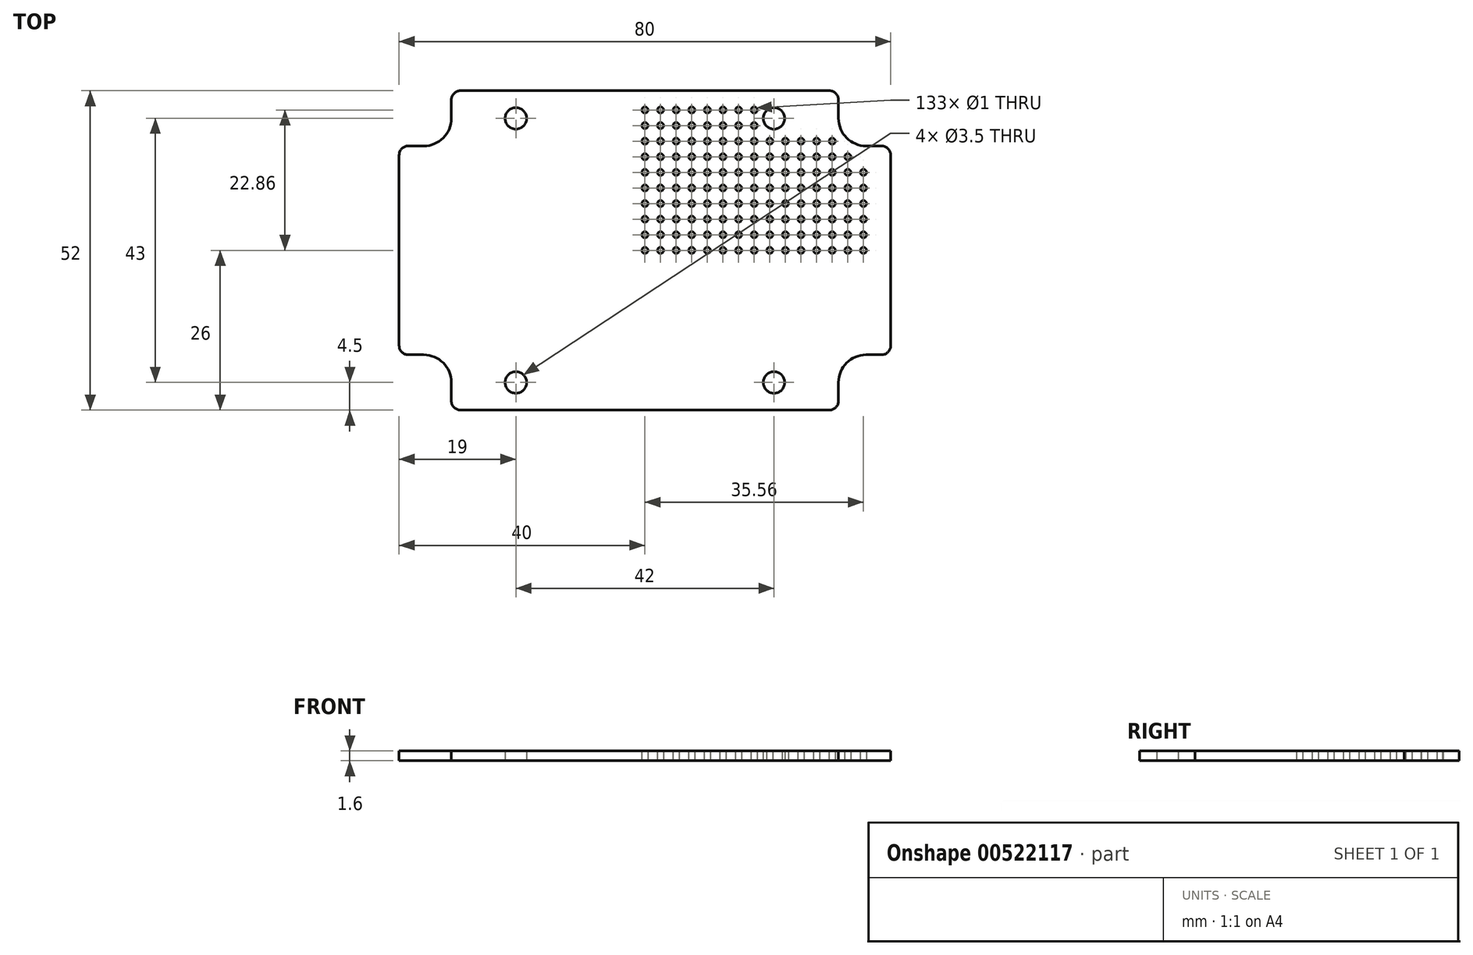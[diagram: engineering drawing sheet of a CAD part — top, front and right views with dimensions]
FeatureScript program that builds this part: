
annotation { "Feature Type Name" : "Feature", "Feature Type Description" : "" }
export const myFeature = defineFeature(function(context is Context, id is Id, definition is map)
    precondition{}
    {
        {
            var Q0;
            Q0=qCreatedBy(makeId("Top.planeOp"),FACE);
            var sketch = newSketch(context, id + "F0", { "sketchPlane" : qUnion([Q0])});
            skLineSegment(sketch, "E0.bottom", {"start": v(-31.5, 26) * mm, "end": v(31.5, 26) * mm});
            skLineSegment(sketch, "E0.top", {"start": v(-31.5, -26) * mm, "end": v(31.5, -26) * mm});
            skLineSegment(sketch, "E0.right", {"start": v(40, 17) * mm, "end": v(40, -17) * mm});
            skPoint(sketch, "E0.middle", {"position": v(0, 0) * mm});
            skLineSegment(sketch, "E1.bottom", {"start": v(-36, 21.5) * mm, "end": v(36, 21.5) * mm, "construction": true});
            skLineSegment(sketch, "E1.top", {"start": v(-36, -21.5) * mm, "end": v(36, -21.5) * mm, "construction": true});
            skLineSegment(sketch, "E1.left", {"start": v(-36, 21.5) * mm, "end": v(-36, -21.5) * mm, "construction": true});
            skLineSegment(sketch, "E1.right", {"start": v(36, 21.5) * mm, "end": v(36, -21.5) * mm, "construction": true});
            skArc(sketch, "E2", {"start": v(31.5, 21.5) * mm, "mid": v(32.82, 18.32) * mm, "end": v(36, 17) * mm});
            skArc(sketch, "E3", {"start": v(36, -17) * mm, "mid": v(32.82, -18.32) * mm, "end": v(31.5, -21.5) * mm});
            skArc(sketch, "E4", {"start": v(-31.5, -21.5) * mm, "mid": v(-32.82, -18.32) * mm, "end": v(-36, -17) * mm});
            skLineSegment(sketch, "E5", {"start": v(31.5, 21.5) * mm, "end": v(31.5, 26) * mm});
            skLineSegment(sketch, "E6", {"start": v(36, 17) * mm, "end": v(40, 17) * mm});
            skPoint(sketch, "E7.orphan", {"position": v(40, 26) * mm});
            skLineSegment(sketch, "E8", {"start": v(36, -17) * mm, "end": v(40, -17) * mm});
            skLineSegment(sketch, "E9", {"start": v(31.5, -21.5) * mm, "end": v(31.5, -26) * mm});
            skPoint(sketch, "E10.orphan", {"position": v(40, -26) * mm});
            skLineSegment(sketch, "E11", {"start": v(-31.5, 21.5) * mm, "end": v(-31.5, 26) * mm});
            skLineSegment(sketch, "E12", {"start": v(-36, 17) * mm, "end": v(-40, 17) * mm});
            skLineSegment(sketch, "E13", {"start": v(-36, -17) * mm, "end": v(-40, -17) * mm});
            skLineSegment(sketch, "E14", {"start": v(-31.5, -21.5) * mm, "end": v(-31.5, -26) * mm});
            skPoint(sketch, "E15.orphan", {"position": v(-40, -26) * mm});
            skArc(sketch, "E16.trimOffspring", {"start": v(-36, 17) * mm, "mid": v(-32.82, 18.32) * mm, "end": v(-31.5, 21.5) * mm});
            skLineSegment(sketch, "E17.trimOffspring", {"start": v(-40, 17) * mm, "end": v(-40, -17) * mm});
            skPoint(sketch, "E0.left.start.orphan", {"position": v(-40, 26) * mm});
            skSolve(sketch);
        }
        {
            var Q0;
            Q0=makeQuery(id+"F0.imprint","IMPRINT",FACE,{"disambiguationData":[TD([[makeQuery(id+"F0.imprint","IMPRINT",EDGE,{"derivedFrom":sQuery(id+"F0.wireOp",EDGE,"E0.bottom")}),-1.0]])]});
            extrude(context, id + "F1", {"entities" : qUnion([Q0]), "depth" : 1.6 * mm, "offsetDistance" : 25 * mm});
        }
        {
            var Q0;
            Q0=makeQuery(id+"F1.opExtrude","SWEPT_EDGE",EDGE,{"disambiguationData":[OSD([sQuery(id+"F0.wireOp",EDGE,"E12"),sQuery(id+"F0.wireOp",EDGE,"E17.trimOffspring")])]});
            var Q1;
            Q1=makeQuery(id+"F1.opExtrude","SWEPT_EDGE",EDGE,{"disambiguationData":[OSD([sQuery(id+"F0.wireOp",EDGE,"E0.bottom"),sQuery(id+"F0.wireOp",EDGE,"E11")])]});
            var Q2;
            Q2=makeQuery(id+"F1.opExtrude","SWEPT_EDGE",EDGE,{"disambiguationData":[OSD([sQuery(id+"F0.wireOp",EDGE,"E13"),sQuery(id+"F0.wireOp",EDGE,"E17.trimOffspring")])]});
            var Q3;
            Q3=makeQuery(id+"F1.opExtrude","SWEPT_EDGE",EDGE,{"disambiguationData":[OSD([sQuery(id+"F0.wireOp",EDGE,"E0.top"),sQuery(id+"F0.wireOp",EDGE,"E14")])]});
            var Q4;
            Q4=makeQuery(id+"F1.opExtrude","SWEPT_EDGE",EDGE,{"disambiguationData":[OSD([sQuery(id+"F0.wireOp",EDGE,"E0.top"),sQuery(id+"F0.wireOp",EDGE,"E9")])]});
            var Q5;
            Q5=makeQuery(id+"F1.opExtrude","SWEPT_EDGE",EDGE,{"disambiguationData":[OSD([sQuery(id+"F0.wireOp",EDGE,"E0.right"),sQuery(id+"F0.wireOp",EDGE,"E8")])]});
            var Q6;
            Q6=makeQuery(id+"F1.opExtrude","SWEPT_EDGE",EDGE,{"disambiguationData":[OSD([sQuery(id+"F0.wireOp",EDGE,"E0.right"),sQuery(id+"F0.wireOp",EDGE,"E6")])]});
            var Q7;
            Q7=makeQuery(id+"F1.opExtrude","SWEPT_EDGE",EDGE,{"disambiguationData":[OSD([sQuery(id+"F0.wireOp",EDGE,"E0.bottom"),sQuery(id+"F0.wireOp",EDGE,"E5")])]});
            fillet(context, id + "F2", {"entities" : qUnion([Q0, Q1, Q2, Q3, Q4, Q5, Q6, Q7]), "radius" : 1.5 * mm, "tangentPropagation" : true, "allowEdgeOverflow" : false});
        }
        {
            var Q0;
            Q0=qCreatedBy(makeId("Top.planeOp"),FACE);
            var sketch = newSketch(context, id + "F3", { "sketchPlane" : qUnion([Q0])});
            skLineSegment(sketch, "E18.bottom", {"start": v(-21, 21.5) * mm, "end": v(21, 21.5) * mm, "construction": true});
            skLineSegment(sketch, "E18.top", {"start": v(-21, -21.5) * mm, "end": v(21, -21.5) * mm, "construction": true});
            skLineSegment(sketch, "E18.left", {"start": v(-21, 21.5) * mm, "end": v(-21, -21.5) * mm, "construction": true});
            skLineSegment(sketch, "E18.right", {"start": v(21, 21.5) * mm, "end": v(21, -21.5) * mm, "construction": true});
            skPoint(sketch, "E18.middle", {"position": v(0, 0) * mm});
            skPoint(sketch, "E19", {"position": v(-21, 21.5) * mm});
            skPoint(sketch, "E20", {"position": v(21, 21.5) * mm});
            skPoint(sketch, "E21", {"position": v(-21, -21.5) * mm});
            skPoint(sketch, "E22", {"position": v(21, -21.5) * mm});
            skPoint(sketch, "E23.0.1.0", {"position": v(0, 2.54) * mm});
            skPoint(sketch, "E23.0.2.0", {"position": v(0, 5.08) * mm});
            skPoint(sketch, "E23.0.3.0", {"position": v(0, 7.62) * mm});
            skPoint(sketch, "E23.0.4.0", {"position": v(0, 10.16) * mm});
            skPoint(sketch, "E23.0.5.0", {"position": v(0, 12.7) * mm});
            skPoint(sketch, "E23.0.6.0", {"position": v(0, 15.24) * mm});
            skPoint(sketch, "E23.0.7.0", {"position": v(0, 17.78) * mm});
            skPoint(sketch, "E23.0.8.0", {"position": v(0, 20.32) * mm});
            skPoint(sketch, "E23.1.0.0", {"position": v(2.54, 0) * mm});
            skPoint(sketch, "E23.1.1.0", {"position": v(2.54, 2.54) * mm});
            skPoint(sketch, "E23.1.2.0", {"position": v(2.54, 5.08) * mm});
            skPoint(sketch, "E23.1.3.0", {"position": v(2.54, 7.62) * mm});
            skPoint(sketch, "E23.1.4.0", {"position": v(2.54, 10.16) * mm});
            skPoint(sketch, "E23.1.5.0", {"position": v(2.54, 12.7) * mm});
            skPoint(sketch, "E23.1.6.0", {"position": v(2.54, 15.24) * mm});
            skPoint(sketch, "E23.1.7.0", {"position": v(2.54, 17.78) * mm});
            skPoint(sketch, "E23.1.8.0", {"position": v(2.54, 20.32) * mm});
            skPoint(sketch, "E23.2.0.0", {"position": v(5.08, 0) * mm});
            skPoint(sketch, "E23.2.1.0", {"position": v(5.08, 2.54) * mm});
            skPoint(sketch, "E23.2.2.0", {"position": v(5.08, 5.08) * mm});
            skPoint(sketch, "E23.2.3.0", {"position": v(5.08, 7.62) * mm});
            skPoint(sketch, "E23.2.4.0", {"position": v(5.08, 10.16) * mm});
            skPoint(sketch, "E23.2.5.0", {"position": v(5.08, 12.7) * mm});
            skPoint(sketch, "E23.2.6.0", {"position": v(5.08, 15.24) * mm});
            skPoint(sketch, "E23.2.7.0", {"position": v(5.08, 17.78) * mm});
            skPoint(sketch, "E23.2.8.0", {"position": v(5.08, 20.32) * mm});
            skLineSegment(sketch, "E23.direction1", {"start": v(0, 0) * mm, "end": v(2.54, 0) * mm, "construction": true});
            skLineSegment(sketch, "E23.direction2", {"start": v(0, 0) * mm, "end": v(0, 2.54) * mm, "construction": true});
            skPoint(sketch, "E24.0.0.9", {"position": v(0, 22.86) * mm});
            skPoint(sketch, "E24.0.1.9", {"position": v(2.54, 22.86) * mm});
            skPoint(sketch, "E24.0.2.9", {"position": v(5.08, 22.86) * mm});
            skPoint(sketch, "E25.0.3.0", {"position": v(7.62, 0) * mm});
            skPoint(sketch, "E25.0.3.1", {"position": v(7.62, 2.54) * mm});
            skPoint(sketch, "E25.0.3.2", {"position": v(7.62, 5.08) * mm});
            skPoint(sketch, "E25.0.3.3", {"position": v(7.62, 7.62) * mm});
            skPoint(sketch, "E25.0.3.4", {"position": v(7.62, 10.16) * mm});
            skPoint(sketch, "E25.0.3.5", {"position": v(7.62, 12.7) * mm});
            skPoint(sketch, "E25.0.3.6", {"position": v(7.62, 15.24) * mm});
            skPoint(sketch, "E25.0.3.7", {"position": v(7.62, 17.78) * mm});
            skPoint(sketch, "E25.0.3.8", {"position": v(7.62, 20.32) * mm});
            skPoint(sketch, "E25.0.3.9", {"position": v(7.62, 22.86) * mm});
            skPoint(sketch, "E25.0.4.0", {"position": v(10.16, 0) * mm});
            skPoint(sketch, "E25.0.4.1", {"position": v(10.16, 2.54) * mm});
            skPoint(sketch, "E25.0.4.2", {"position": v(10.16, 5.08) * mm});
            skPoint(sketch, "E25.0.4.3", {"position": v(10.16, 7.62) * mm});
            skPoint(sketch, "E25.0.4.4", {"position": v(10.16, 10.16) * mm});
            skPoint(sketch, "E25.0.4.5", {"position": v(10.16, 12.7) * mm});
            skPoint(sketch, "E25.0.4.6", {"position": v(10.16, 15.24) * mm});
            skPoint(sketch, "E25.0.4.7", {"position": v(10.16, 17.78) * mm});
            skPoint(sketch, "E25.0.4.8", {"position": v(10.16, 20.32) * mm});
            skPoint(sketch, "E25.0.4.9", {"position": v(10.16, 22.86) * mm});
            skPoint(sketch, "E25.0.5.0", {"position": v(12.7, 0) * mm});
            skPoint(sketch, "E25.0.5.1", {"position": v(12.7, 2.54) * mm});
            skPoint(sketch, "E25.0.5.2", {"position": v(12.7, 5.08) * mm});
            skPoint(sketch, "E25.0.5.3", {"position": v(12.7, 7.62) * mm});
            skPoint(sketch, "E25.0.5.4", {"position": v(12.7, 10.16) * mm});
            skPoint(sketch, "E25.0.5.5", {"position": v(12.7, 12.7) * mm});
            skPoint(sketch, "E25.0.5.6", {"position": v(12.7, 15.24) * mm});
            skPoint(sketch, "E25.0.5.7", {"position": v(12.7, 17.78) * mm});
            skPoint(sketch, "E25.0.5.8", {"position": v(12.7, 20.32) * mm});
            skPoint(sketch, "E25.0.5.9", {"position": v(12.7, 22.86) * mm});
            skPoint(sketch, "E25.0.6.0", {"position": v(15.24, 0) * mm});
            skPoint(sketch, "E25.0.6.1", {"position": v(15.24, 2.54) * mm});
            skPoint(sketch, "E25.0.6.2", {"position": v(15.24, 5.08) * mm});
            skPoint(sketch, "E25.0.6.3", {"position": v(15.24, 7.62) * mm});
            skPoint(sketch, "E25.0.6.4", {"position": v(15.24, 10.16) * mm});
            skPoint(sketch, "E25.0.6.5", {"position": v(15.24, 12.7) * mm});
            skPoint(sketch, "E25.0.6.6", {"position": v(15.24, 15.24) * mm});
            skPoint(sketch, "E25.0.6.7", {"position": v(15.24, 17.78) * mm});
            skPoint(sketch, "E25.0.6.8", {"position": v(15.24, 20.32) * mm});
            skPoint(sketch, "E25.0.6.9", {"position": v(15.24, 22.86) * mm});
            skPoint(sketch, "E25.0.7.0", {"position": v(17.78, 0) * mm});
            skPoint(sketch, "E25.0.7.1", {"position": v(17.78, 2.54) * mm});
            skPoint(sketch, "E25.0.7.2", {"position": v(17.78, 5.08) * mm});
            skPoint(sketch, "E25.0.7.3", {"position": v(17.78, 7.62) * mm});
            skPoint(sketch, "E25.0.7.4", {"position": v(17.78, 10.16) * mm});
            skPoint(sketch, "E25.0.7.5", {"position": v(17.78, 12.7) * mm});
            skPoint(sketch, "E25.0.7.6", {"position": v(17.78, 15.24) * mm});
            skPoint(sketch, "E25.0.7.7", {"position": v(17.78, 17.78) * mm});
            skPoint(sketch, "E25.0.7.8", {"position": v(17.78, 20.32) * mm});
            skPoint(sketch, "E25.0.7.9", {"position": v(17.78, 22.86) * mm});
            skPoint(sketch, "E25.0.8.0", {"position": v(20.32, 0) * mm});
            skPoint(sketch, "E25.0.8.1", {"position": v(20.32, 2.54) * mm});
            skPoint(sketch, "E25.0.8.2", {"position": v(20.32, 5.08) * mm});
            skPoint(sketch, "E25.0.8.3", {"position": v(20.32, 7.62) * mm});
            skPoint(sketch, "E25.0.8.4", {"position": v(20.32, 10.16) * mm});
            skPoint(sketch, "E25.0.8.5", {"position": v(20.32, 12.7) * mm});
            skPoint(sketch, "E25.0.8.6", {"position": v(20.32, 15.24) * mm});
            skPoint(sketch, "E25.0.8.7", {"position": v(20.32, 17.78) * mm});
            skPoint(sketch, "E25.0.8.8", {"position": v(20.32, 20.32) * mm});
            skPoint(sketch, "E25.0.8.9", {"position": v(20.32, 22.86) * mm});
            skPoint(sketch, "E25.0.9.0", {"position": v(22.86, 0) * mm});
            skPoint(sketch, "E25.0.9.1", {"position": v(22.86, 2.54) * mm});
            skPoint(sketch, "E25.0.9.2", {"position": v(22.86, 5.08) * mm});
            skPoint(sketch, "E25.0.9.3", {"position": v(22.86, 7.62) * mm});
            skPoint(sketch, "E25.0.9.4", {"position": v(22.86, 10.16) * mm});
            skPoint(sketch, "E25.0.9.5", {"position": v(22.86, 12.7) * mm});
            skPoint(sketch, "E25.0.9.6", {"position": v(22.86, 15.24) * mm});
            skPoint(sketch, "E25.0.9.7", {"position": v(22.86, 17.78) * mm});
            skPoint(sketch, "E25.0.9.8", {"position": v(22.86, 20.32) * mm});
            skPoint(sketch, "E25.0.9.9", {"position": v(22.86, 22.86) * mm});
            skPoint(sketch, "E25.0.10.0", {"position": v(25.4, 0) * mm});
            skPoint(sketch, "E25.0.10.1", {"position": v(25.4, 2.54) * mm});
            skPoint(sketch, "E25.0.10.2", {"position": v(25.4, 5.08) * mm});
            skPoint(sketch, "E25.0.10.3", {"position": v(25.4, 7.62) * mm});
            skPoint(sketch, "E25.0.10.4", {"position": v(25.4, 10.16) * mm});
            skPoint(sketch, "E25.0.10.5", {"position": v(25.4, 12.7) * mm});
            skPoint(sketch, "E25.0.10.6", {"position": v(25.4, 15.24) * mm});
            skPoint(sketch, "E25.0.10.7", {"position": v(25.4, 17.78) * mm});
            skPoint(sketch, "E25.0.10.8", {"position": v(25.4, 20.32) * mm});
            skPoint(sketch, "E25.0.10.9", {"position": v(25.4, 22.86) * mm});
            skPoint(sketch, "E25.0.11.0", {"position": v(27.94, 0) * mm});
            skPoint(sketch, "E25.0.11.1", {"position": v(27.94, 2.54) * mm});
            skPoint(sketch, "E25.0.11.2", {"position": v(27.94, 5.08) * mm});
            skPoint(sketch, "E25.0.11.3", {"position": v(27.94, 7.62) * mm});
            skPoint(sketch, "E25.0.11.4", {"position": v(27.94, 10.16) * mm});
            skPoint(sketch, "E25.0.11.5", {"position": v(27.94, 12.7) * mm});
            skPoint(sketch, "E25.0.11.6", {"position": v(27.94, 15.24) * mm});
            skPoint(sketch, "E25.0.11.7", {"position": v(27.94, 17.78) * mm});
            skPoint(sketch, "E25.0.11.8", {"position": v(27.94, 20.32) * mm});
            skPoint(sketch, "E25.0.11.9", {"position": v(27.94, 22.86) * mm});
            skPoint(sketch, "E25.0.12.0", {"position": v(30.48, 0) * mm});
            skPoint(sketch, "E25.0.12.1", {"position": v(30.48, 2.54) * mm});
            skPoint(sketch, "E25.0.12.2", {"position": v(30.48, 5.08) * mm});
            skPoint(sketch, "E25.0.12.3", {"position": v(30.48, 7.62) * mm});
            skPoint(sketch, "E25.0.12.4", {"position": v(30.48, 10.16) * mm});
            skPoint(sketch, "E25.0.12.5", {"position": v(30.48, 12.7) * mm});
            skPoint(sketch, "E25.0.12.6", {"position": v(30.48, 15.24) * mm});
            skPoint(sketch, "E25.0.12.7", {"position": v(30.48, 17.78) * mm});
            skPoint(sketch, "E25.0.12.8", {"position": v(30.48, 20.32) * mm});
            skPoint(sketch, "E25.0.12.9", {"position": v(30.48, 22.86) * mm});
            skPoint(sketch, "E26.0.13.0", {"position": v(33.02, 0) * mm});
            skPoint(sketch, "E26.0.13.1", {"position": v(33.02, 2.54) * mm});
            skPoint(sketch, "E26.0.13.2", {"position": v(33.02, 5.08) * mm});
            skPoint(sketch, "E26.0.13.3", {"position": v(33.02, 7.62) * mm});
            skPoint(sketch, "E26.0.13.4", {"position": v(33.02, 10.16) * mm});
            skPoint(sketch, "E26.0.13.5", {"position": v(33.02, 12.7) * mm});
            skPoint(sketch, "E26.0.13.6", {"position": v(33.02, 15.24) * mm});
            skPoint(sketch, "E26.0.13.7", {"position": v(33.02, 17.78) * mm});
            skPoint(sketch, "E26.0.13.8", {"position": v(33.02, 20.32) * mm});
            skPoint(sketch, "E26.0.13.9", {"position": v(33.02, 22.86) * mm});
            skPoint(sketch, "E26.0.14.0", {"position": v(35.56, 0) * mm});
            skPoint(sketch, "E26.0.14.1", {"position": v(35.56, 2.54) * mm});
            skPoint(sketch, "E26.0.14.2", {"position": v(35.56, 5.08) * mm});
            skPoint(sketch, "E26.0.14.3", {"position": v(35.56, 7.62) * mm});
            skPoint(sketch, "E26.0.14.4", {"position": v(35.56, 10.16) * mm});
            skPoint(sketch, "E26.0.14.5", {"position": v(35.56, 12.7) * mm});
            skPoint(sketch, "E26.0.14.6", {"position": v(35.56, 15.24) * mm});
            skPoint(sketch, "E26.0.14.7", {"position": v(35.56, 17.78) * mm});
            skPoint(sketch, "E26.0.14.8", {"position": v(35.56, 20.32) * mm});
            skPoint(sketch, "E26.0.14.9", {"position": v(35.56, 22.86) * mm});
            skSolve(sketch);
        }
        {
            var Q0;
            Q0=sQuery(id+"F3.wireOp",VERTEX,"E20");
            var Q1;
            Q1=sQuery(id+"F3.wireOp",VERTEX,"E22");
            var Q2;
            Q2=sQuery(id+"F3.wireOp",VERTEX,"E21");
            var Q3;
            Q3=sQuery(id+"F3.wireOp",VERTEX,"E19");
            var Q4;
            Q4=makeQuery(id+"F1.opExtrude","SWEPT_BODY",BODY,{"disambiguationData":[OSD([sQuery(id+"F0.wireOp",EDGE,"E0.bottom"),sQuery(id+"F0.wireOp",EDGE,"E0.top"),sQuery(id+"F0.wireOp",EDGE,"E0.right"),sQuery(id+"F0.wireOp",EDGE,"E2"),sQuery(id+"F0.wireOp",EDGE,"E3"),sQuery(id+"F0.wireOp",EDGE,"E4"),sQuery(id+"F0.wireOp",EDGE,"E5"),sQuery(id+"F0.wireOp",EDGE,"E6"),sQuery(id+"F0.wireOp",EDGE,"E8"),sQuery(id+"F0.wireOp",EDGE,"E9"),sQuery(id+"F0.wireOp",EDGE,"E11"),sQuery(id+"F0.wireOp",EDGE,"E12"),sQuery(id+"F0.wireOp",EDGE,"E13"),sQuery(id+"F0.wireOp",EDGE,"E14"),sQuery(id+"F0.wireOp",EDGE,"E16.trimOffspring"),sQuery(id+"F0.wireOp",EDGE,"E17.trimOffspring")])]});
            hole(context, id + "F4", {"style" : HoleStyle.SIMPLE, "endStyle" : HoleEndStyle.THROUGH, "oppositeDirection" : true, "holeDiameter" : 3.5 * mm, "isTappedThrough" : true, "tappedDepth" : 12 * mm, "tapClearance" : 3, "startFromSketch" : true, "locations" : qUnion([Q0, Q1, Q2, Q3]), "scope" : qUnion([Q4])});
        }
        {
            var Q0;
            Q0=sQuery(id+"F3.wireOp",VERTEX,"E25.0.4.5");
            var Q1;
            Q1=sQuery(id+"F3.wireOp",VERTEX,"E25.0.5.2");
            var Q2;
            Q2=sQuery(id+"F3.wireOp",VERTEX,"E24.0.2.9");
            var Q3;
            Q3=sQuery(id+"F3.wireOp",VERTEX,"E25.0.3.6");
            var Q4;
            Q4=sQuery(id+"F3.wireOp",VERTEX,"E23.1.4.0");
            var Q5;
            Q5=sQuery(id+"F3.wireOp",VERTEX,"E23.2.2.0");
            var Q6;
            Q6=sQuery(id+"F3.wireOp",VERTEX,"E23.0.4.0");
            var Q7;
            Q7=sQuery(id+"F3.wireOp",VERTEX,"E25.0.7.7");
            var Q8;
            Q8=sQuery(id+"F3.wireOp",VERTEX,"E25.0.6.8");
            var Q9;
            Q9=sQuery(id+"F3.wireOp",VERTEX,"E25.0.6.1");
            var Q10;
            Q10=sQuery(id+"F3.wireOp",VERTEX,"E24.0.0.9");
            var Q11;
            Q11=sQuery(id+"F3.wireOp",VERTEX,"E23.1.2.0");
            var Q12;
            Q12=sQuery(id+"F3.wireOp",VERTEX,"E25.0.7.5");
            var Q13;
            Q13=sQuery(id+"F3.wireOp",VERTEX,"E25.0.5.9");
            var Q14;
            Q14=sQuery(id+"F3.wireOp",VERTEX,"E25.0.4.3");
            var Q15;
            Q15=sQuery(id+"F3.wireOp",VERTEX,"E25.0.4.6");
            var Q16;
            Q16=sQuery(id+"F3.wireOp",VERTEX,"E25.0.5.3");
            var Q17;
            Q17=sQuery(id+"F3.wireOp",VERTEX,"E25.0.3.7");
            var Q18;
            Q18=sQuery(id+"F3.wireOp",VERTEX,"E25.0.3.0");
            var Q19;
            Q19=sQuery(id+"F3.wireOp",VERTEX,"E23.1.5.0");
            var Q20;
            Q20=sQuery(id+"F3.wireOp",VERTEX,"E23.2.3.0");
            var Q21;
            Q21=sQuery(id+"F3.wireOp",VERTEX,"E23.0.5.0");
            var Q22;
            Q22=sQuery(id+"F3.wireOp",VERTEX,"E25.0.7.8");
            var Q23;
            Q23=sQuery(id+"F3.wireOp",VERTEX,"E25.0.6.2");
            var Q24;
            Q24=sQuery(id+"F3.wireOp",VERTEX,"E25.0.6.9");
            var Q25;
            Q25=sQuery(id+"F3.wireOp",VERTEX,"E25.0.7.0");
            var Q26;
            Q26=sQuery(id+"F3.wireOp",VERTEX,"E25.0.5.4");
            var Q27;
            Q27=sQuery(id+"F3.wireOp",VERTEX,"E25.0.3.8");
            var Q28;
            Q28=sQuery(id+"F3.wireOp",VERTEX,"E25.0.4.7");
            var Q29;
            Q29=sQuery(id+"F3.wireOp",VERTEX,"E25.0.3.1");
            var Q30;
            Q30=sQuery(id+"F3.wireOp",VERTEX,"E23.1.6.0");
            var Q31;
            Q31=sQuery(id+"F3.wireOp",VERTEX,"E25.0.7.9");
            var Q32;
            Q32=sQuery(id+"F3.wireOp",VERTEX,"E25.0.6.3");
            var Q33;
            Q33=sQuery(id+"F3.wireOp",VERTEX,"E23.2.4.0");
            var Q34;
            Q34=sQuery(id+"F3.wireOp",VERTEX,"E23.0.6.0");
            var Q35;
            Q35=sQuery(id+"F3.wireOp",VERTEX,"E25.0.4.8");
            var Q36;
            Q36=sQuery(id+"F3.wireOp",VERTEX,"E25.0.3.2");
            var Q37;
            Q37=sQuery(id+"F3.wireOp",VERTEX,"E23.1.7.0");
            var Q38;
            Q38=sQuery(id+"F3.wireOp",VERTEX,"E25.0.6.4");
            var Q39;
            Q39=sQuery(id+"F3.wireOp",VERTEX,"E23.2.5.0");
            var Q40;
            Q40=sQuery(id+"F3.wireOp",VERTEX,"E23.0.7.0");
            var Q41;
            Q41=sQuery(id+"F3.wireOp",VERTEX,"E25.0.7.1");
            var Q42;
            Q42=sQuery(id+"F3.wireOp",VERTEX,"E25.0.5.5");
            var Q43;
            Q43=sQuery(id+"F3.wireOp",VERTEX,"E25.0.3.9");
            var Q44;
            Q44=sQuery(id+"F3.wireOp",VERTEX,"E25.0.4.9");
            var Q45;
            Q45=sQuery(id+"F3.wireOp",VERTEX,"E25.0.3.3");
            var Q46;
            Q46=sQuery(id+"F3.wireOp",VERTEX,"E23.1.8.0");
            var Q47;
            Q47=sQuery(id+"F3.wireOp",VERTEX,"E23.0.1.0");
            var Q48;
            Q48=sQuery(id+"F3.wireOp",VERTEX,"E25.0.6.5");
            var Q49;
            Q49=sQuery(id+"F3.wireOp",VERTEX,"E23.2.6.0");
            var Q50;
            Q50=sQuery(id+"F3.wireOp",VERTEX,"E23.0.8.0");
            var Q51;
            Q51=sQuery(id+"F3.wireOp",VERTEX,"E25.0.7.2");
            var Q52;
            Q52=sQuery(id+"F3.wireOp",VERTEX,"E25.0.5.6");
            var Q53;
            Q53=sQuery(id+"F3.wireOp",VERTEX,"E25.0.4.0");
            var Q54;
            Q54=sQuery(id+"F3.wireOp",VERTEX,"E25.0.5.0");
            var Q55;
            Q55=sQuery(id+"F3.wireOp",VERTEX,"E25.0.3.4");
            var Q56;
            Q56=sQuery(id+"F3.wireOp",VERTEX,"E23.2.0.0");
            var Q57;
            Q57=sQuery(id+"F3.wireOp",VERTEX,"E23.0.2.0");
            var Q58;
            Q58=sQuery(id+"F3.wireOp",VERTEX,"E25.0.6.6");
            var Q59;
            Q59=sQuery(id+"F3.wireOp",VERTEX,"E23.direction1.end");
            var Q60;
            Q60=sQuery(id+"F3.wireOp",VERTEX,"E23.direction2.start");
            var Q61;
            Q61=sQuery(id+"F3.wireOp",VERTEX,"E23.2.7.0");
            var Q62;
            Q62=sQuery(id+"F3.wireOp",VERTEX,"E25.0.7.3");
            var Q63;
            Q63=sQuery(id+"F3.wireOp",VERTEX,"E25.0.5.7");
            var Q64;
            Q64=sQuery(id+"F3.wireOp",VERTEX,"E25.0.4.1");
            var Q65;
            Q65=sQuery(id+"F3.wireOp",VERTEX,"E25.0.5.1");
            var Q66;
            Q66=sQuery(id+"F3.wireOp",VERTEX,"E25.0.4.4");
            var Q67;
            Q67=sQuery(id+"F3.wireOp",VERTEX,"E24.0.1.9");
            var Q68;
            Q68=sQuery(id+"F3.wireOp",VERTEX,"E25.0.3.5");
            var Q69;
            Q69=sQuery(id+"F3.wireOp",VERTEX,"E23.2.1.0");
            var Q70;
            Q70=sQuery(id+"F3.wireOp",VERTEX,"E23.1.3.0");
            var Q71;
            Q71=sQuery(id+"F3.wireOp",VERTEX,"E23.0.3.0");
            var Q72;
            Q72=sQuery(id+"F3.wireOp",VERTEX,"E25.0.7.6");
            var Q73;
            Q73=sQuery(id+"F3.wireOp",VERTEX,"E25.0.6.0");
            var Q74;
            Q74=sQuery(id+"F3.wireOp",VERTEX,"E25.0.6.7");
            var Q75;
            Q75=sQuery(id+"F3.wireOp",VERTEX,"E23.2.8.0");
            var Q76;
            Q76=sQuery(id+"F3.wireOp",VERTEX,"E23.1.1.0");
            var Q77;
            Q77=sQuery(id+"F3.wireOp",VERTEX,"E25.0.7.4");
            var Q78;
            Q78=sQuery(id+"F3.wireOp",VERTEX,"E25.0.5.8");
            var Q79;
            Q79=sQuery(id+"F3.wireOp",VERTEX,"E25.0.4.2");
            var Q80;
            Q80=makeQuery(id+"F1.opExtrude","SWEPT_BODY",BODY,{"disambiguationData":[OSD([sQuery(id+"F0.wireOp",EDGE,"E0.bottom"),sQuery(id+"F0.wireOp",EDGE,"E0.top"),sQuery(id+"F0.wireOp",EDGE,"E0.right"),sQuery(id+"F0.wireOp",EDGE,"E2"),sQuery(id+"F0.wireOp",EDGE,"E3"),sQuery(id+"F0.wireOp",EDGE,"E4"),sQuery(id+"F0.wireOp",EDGE,"E5"),sQuery(id+"F0.wireOp",EDGE,"E6"),sQuery(id+"F0.wireOp",EDGE,"E8"),sQuery(id+"F0.wireOp",EDGE,"E9"),sQuery(id+"F0.wireOp",EDGE,"E11"),sQuery(id+"F0.wireOp",EDGE,"E12"),sQuery(id+"F0.wireOp",EDGE,"E13"),sQuery(id+"F0.wireOp",EDGE,"E14"),sQuery(id+"F0.wireOp",EDGE,"E16.trimOffspring"),sQuery(id+"F0.wireOp",EDGE,"E17.trimOffspring")])]});
            hole(context, id + "F5", {"style" : HoleStyle.SIMPLE, "endStyle" : HoleEndStyle.THROUGH, "oppositeDirection" : true, "holeDiameter" : 1 * mm, "isTappedThrough" : true, "tappedDepth" : 12 * mm, "tapClearance" : 3, "startFromSketch" : true, "locations" : qUnion([Q0, Q1, Q2, Q3, Q4, Q5, Q6, Q7, Q8, Q9, Q10, Q11, Q12, Q13, Q14, Q15, Q16, Q17, Q18, Q19, Q20, Q21, Q22, Q23, Q24, Q25, Q26, Q27, Q28, Q29, Q30, Q31, Q32, Q33, Q34, Q35, Q36, Q37, Q38, Q39, Q40, Q41, Q42, Q43, Q44, Q45, Q46, Q47, Q48, Q49, Q50, Q51, Q52, Q53, Q54, Q55, Q56, Q57, Q58, Q59, Q60, Q61, Q62, Q63, Q64, Q65, Q66, Q67, Q68, Q69, Q70, Q71, Q72, Q73, Q74, Q75, Q76, Q77, Q78, Q79]), "scope" : qUnion([Q80])});
        }
        {
            var Q0;
            Q0=sQuery(id+"F3.wireOp",VERTEX,"E26.0.14.1");
            var Q1;
            Q1=sQuery(id+"F3.wireOp",VERTEX,"E26.0.14.2");
            var Q2;
            Q2=sQuery(id+"F3.wireOp",VERTEX,"E26.0.14.3");
            var Q3;
            Q3=sQuery(id+"F3.wireOp",VERTEX,"E26.0.14.4");
            var Q4;
            Q4=sQuery(id+"F3.wireOp",VERTEX,"E26.0.14.5");
            var Q5;
            Q5=sQuery(id+"F3.wireOp",VERTEX,"E26.0.14.0");
            var Q6;
            Q6=sQuery(id+"F3.wireOp",VERTEX,"E26.0.13.2");
            var Q7;
            Q7=sQuery(id+"F3.wireOp",VERTEX,"E26.0.13.3");
            var Q8;
            Q8=sQuery(id+"F3.wireOp",VERTEX,"E26.0.13.4");
            var Q9;
            Q9=sQuery(id+"F3.wireOp",VERTEX,"E26.0.13.5");
            var Q10;
            Q10=sQuery(id+"F3.wireOp",VERTEX,"E26.0.13.6");
            var Q11;
            Q11=sQuery(id+"F3.wireOp",VERTEX,"E26.0.13.0");
            var Q12;
            Q12=sQuery(id+"F3.wireOp",VERTEX,"E26.0.13.1");
            var Q13;
            Q13=sQuery(id+"F3.wireOp",VERTEX,"E25.0.11.6");
            var Q14;
            Q14=sQuery(id+"F3.wireOp",VERTEX,"E25.0.10.0");
            var Q15;
            Q15=sQuery(id+"F3.wireOp",VERTEX,"E25.0.9.3");
            var Q16;
            Q16=sQuery(id+"F3.wireOp",VERTEX,"E25.0.8.4");
            var Q17;
            Q17=sQuery(id+"F3.wireOp",VERTEX,"E25.0.12.5");
            var Q18;
            Q18=sQuery(id+"F3.wireOp",VERTEX,"E25.0.9.1");
            var Q19;
            Q19=sQuery(id+"F3.wireOp",VERTEX,"E25.0.12.3");
            var Q20;
            Q20=sQuery(id+"F3.wireOp",VERTEX,"E25.0.10.7");
            var Q21;
            Q21=sQuery(id+"F3.wireOp",VERTEX,"E25.0.11.7");
            var Q22;
            Q22=sQuery(id+"F3.wireOp",VERTEX,"E25.0.11.0");
            var Q23;
            Q23=sQuery(id+"F3.wireOp",VERTEX,"E25.0.10.1");
            var Q24;
            Q24=sQuery(id+"F3.wireOp",VERTEX,"E25.0.9.4");
            var Q25;
            Q25=sQuery(id+"F3.wireOp",VERTEX,"E25.0.8.5");
            var Q26;
            Q26=sQuery(id+"F3.wireOp",VERTEX,"E25.0.12.6");
            var Q27;
            Q27=sQuery(id+"F3.wireOp",VERTEX,"E25.0.8.6");
            var Q28;
            Q28=sQuery(id+"F3.wireOp",VERTEX,"E25.0.10.2");
            var Q29;
            Q29=sQuery(id+"F3.wireOp",VERTEX,"E25.0.11.1");
            var Q30;
            Q30=sQuery(id+"F3.wireOp",VERTEX,"E25.0.9.5");
            var Q31;
            Q31=sQuery(id+"F3.wireOp",VERTEX,"E25.0.12.7");
            var Q32;
            Q32=sQuery(id+"F3.wireOp",VERTEX,"E25.0.10.3");
            var Q33;
            Q33=sQuery(id+"F3.wireOp",VERTEX,"E25.0.11.2");
            var Q34;
            Q34=sQuery(id+"F3.wireOp",VERTEX,"E25.0.9.6");
            var Q35;
            Q35=sQuery(id+"F3.wireOp",VERTEX,"E25.0.8.0");
            var Q36;
            Q36=sQuery(id+"F3.wireOp",VERTEX,"E25.0.8.7");
            var Q37;
            Q37=sQuery(id+"F3.wireOp",VERTEX,"E25.0.11.3");
            var Q38;
            Q38=sQuery(id+"F3.wireOp",VERTEX,"E25.0.9.7");
            var Q39;
            Q39=sQuery(id+"F3.wireOp",VERTEX,"E25.0.8.1");
            var Q40;
            Q40=sQuery(id+"F3.wireOp",VERTEX,"E25.0.12.0");
            var Q41;
            Q41=sQuery(id+"F3.wireOp",VERTEX,"E25.0.10.4");
            var Q42;
            Q42=sQuery(id+"F3.wireOp",VERTEX,"E25.0.11.4");
            var Q43;
            Q43=sQuery(id+"F3.wireOp",VERTEX,"E25.0.8.2");
            var Q44;
            Q44=sQuery(id+"F3.wireOp",VERTEX,"E25.0.12.1");
            var Q45;
            Q45=sQuery(id+"F3.wireOp",VERTEX,"E25.0.10.5");
            var Q46;
            Q46=sQuery(id+"F3.wireOp",VERTEX,"E25.0.11.5");
            var Q47;
            Q47=sQuery(id+"F3.wireOp",VERTEX,"E25.0.9.2");
            var Q48;
            Q48=sQuery(id+"F3.wireOp",VERTEX,"E25.0.8.3");
            var Q49;
            Q49=sQuery(id+"F3.wireOp",VERTEX,"E25.0.12.4");
            var Q50;
            Q50=sQuery(id+"F3.wireOp",VERTEX,"E25.0.9.0");
            var Q51;
            Q51=sQuery(id+"F3.wireOp",VERTEX,"E25.0.12.2");
            var Q52;
            Q52=sQuery(id+"F3.wireOp",VERTEX,"E25.0.10.6");
            var Q53;
            Q53=makeQuery(id+"F1.opExtrude","SWEPT_BODY",BODY,{"disambiguationData":[OSD([sQuery(id+"F0.wireOp",EDGE,"E0.bottom"),sQuery(id+"F0.wireOp",EDGE,"E0.top"),sQuery(id+"F0.wireOp",EDGE,"E0.right"),sQuery(id+"F0.wireOp",EDGE,"E2"),sQuery(id+"F0.wireOp",EDGE,"E3"),sQuery(id+"F0.wireOp",EDGE,"E4"),sQuery(id+"F0.wireOp",EDGE,"E5"),sQuery(id+"F0.wireOp",EDGE,"E6"),sQuery(id+"F0.wireOp",EDGE,"E8"),sQuery(id+"F0.wireOp",EDGE,"E9"),sQuery(id+"F0.wireOp",EDGE,"E11"),sQuery(id+"F0.wireOp",EDGE,"E12"),sQuery(id+"F0.wireOp",EDGE,"E13"),sQuery(id+"F0.wireOp",EDGE,"E14"),sQuery(id+"F0.wireOp",EDGE,"E16.trimOffspring"),sQuery(id+"F0.wireOp",EDGE,"E17.trimOffspring")])]});
            hole(context, id + "F6", {"style" : HoleStyle.SIMPLE, "endStyle" : HoleEndStyle.THROUGH, "oppositeDirection" : true, "holeDiameter" : 1 * mm, "isTappedThrough" : true, "tappedDepth" : 12 * mm, "tapClearance" : 3, "startFromSketch" : true, "locations" : qUnion([Q0, Q1, Q2, Q3, Q4, Q5, Q6, Q7, Q8, Q9, Q10, Q11, Q12, Q13, Q14, Q15, Q16, Q17, Q18, Q19, Q20, Q21, Q22, Q23, Q24, Q25, Q26, Q27, Q28, Q29, Q30, Q31, Q32, Q33, Q34, Q35, Q36, Q37, Q38, Q39, Q40, Q41, Q42, Q43, Q44, Q45, Q46, Q47, Q48, Q49, Q50, Q51, Q52]), "scope" : qUnion([Q53])});
        }
    });
